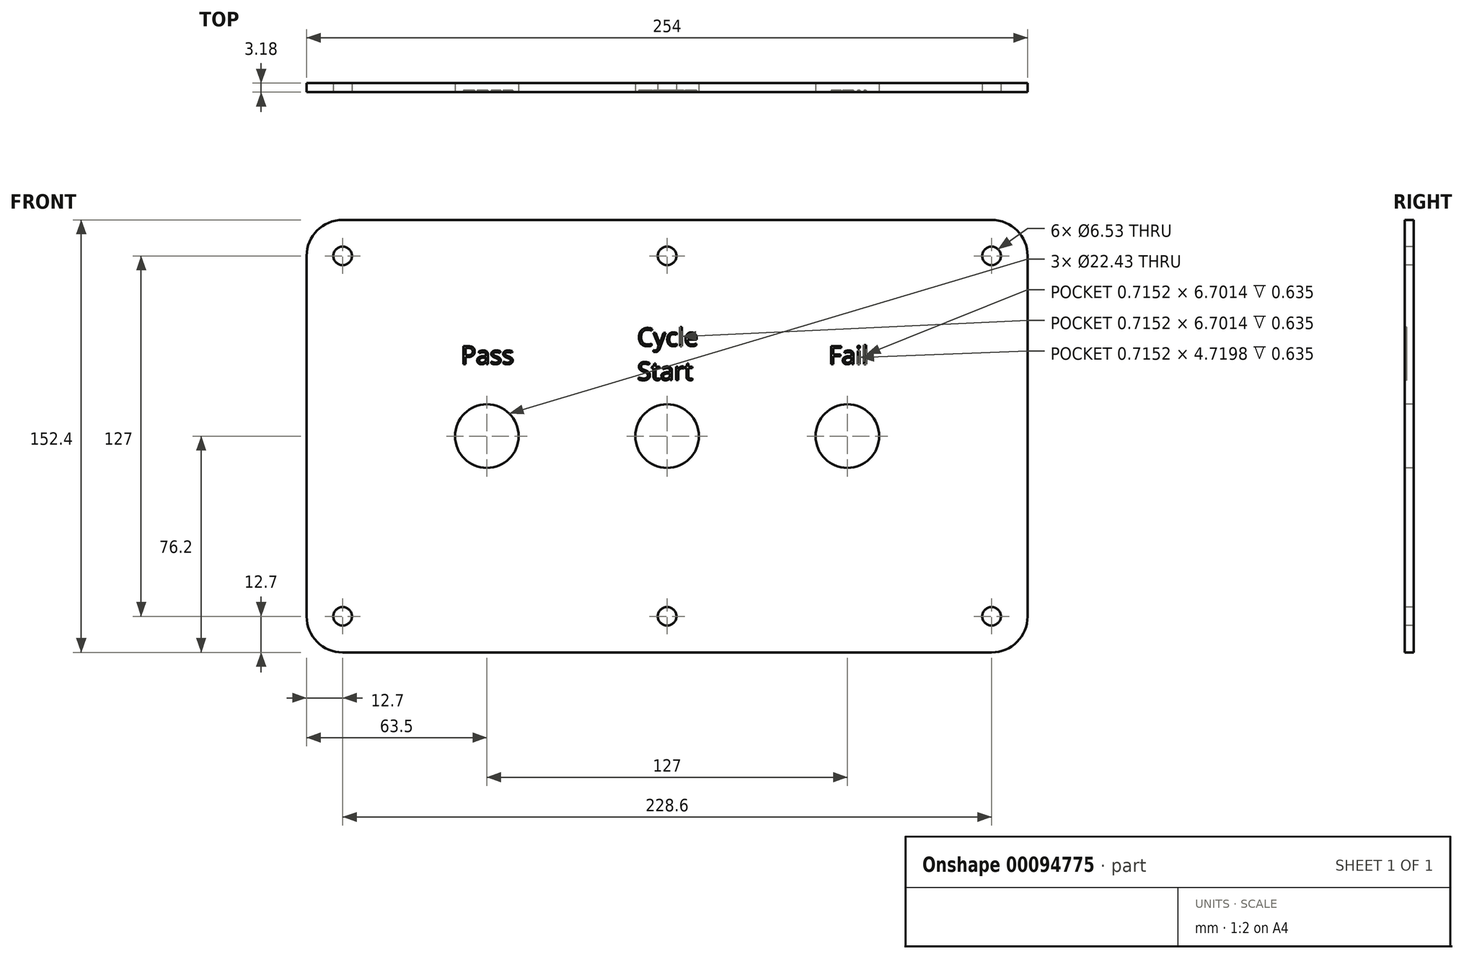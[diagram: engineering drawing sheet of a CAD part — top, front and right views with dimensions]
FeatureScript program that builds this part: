
annotation { "Feature Type Name" : "Feature", "Feature Type Description" : "" }
export const myFeature = defineFeature(function(context is Context, id is Id, definition is map)
    precondition{}
    {
        {
            var Q0;
            Q0=qCreatedBy(makeId("Front.planeOp"),FACE);
            var sketch = newSketch(context, id + "F0", { "sketchPlane" : qUnion([Q0])});
            skLineSegment(sketch, "E0.bottom", {"start": v(-114.3, 76.2) * mm, "end": v(114.3, 76.2) * mm});
            skLineSegment(sketch, "E0.top", {"start": v(-114.3, -76.2) * mm, "end": v(114.3, -76.2) * mm});
            skLineSegment(sketch, "E0.left", {"start": v(-127, 63.5) * mm, "end": v(-127, -63.5) * mm});
            skLineSegment(sketch, "E0.right", {"start": v(127, 63.5) * mm, "end": v(127, -63.5) * mm});
            skPoint(sketch, "E0.middle", {"position": v(0, 0) * mm});
            skPoint(sketch, "E1.visualSharp", {"position": v(-127, 76.2) * mm});
            skArc(sketch, "E1.filletArc", {"start": v(-114.3, 76.2) * mm, "mid": v(-123.28, 72.48) * mm, "end": v(-127, 63.5) * mm});
            skPoint(sketch, "E2.visualSharp", {"position": v(127, 76.2) * mm});
            skArc(sketch, "E2.filletArc", {"start": v(127, 63.5) * mm, "mid": v(123.28, 72.48) * mm, "end": v(114.3, 76.2) * mm});
            skPoint(sketch, "E3.visualSharp", {"position": v(127, -76.2) * mm});
            skArc(sketch, "E3.filletArc", {"start": v(114.3, -76.2) * mm, "mid": v(123.28, -72.48) * mm, "end": v(127, -63.5) * mm});
            skPoint(sketch, "E4.visualSharp", {"position": v(-127, -76.2) * mm});
            skArc(sketch, "E4.filletArc", {"start": v(-127, -63.5) * mm, "mid": v(-123.28, -72.48) * mm, "end": v(-114.3, -76.2) * mm});
            skSolve(sketch);
        }
        {
            var Q0;
            Q0=qSketchRegion(id+"F0",true);
            extrude(context, id + "F1", {"entities" : qUnion([Q0]), "depth" : 3.17 * mm});
        }
        {
            var Q0;
            Q0=makeQuery(id+"F1.opExtrude","CAP_FACE",FACE,{"disambiguationData":[OSD([sQuery(id+"F0.wireOp",EDGE,"E0.bottom"),sQuery(id+"F0.wireOp",EDGE,"E0.top"),sQuery(id+"F0.wireOp",EDGE,"E0.left"),sQuery(id+"F0.wireOp",EDGE,"E0.right")])],"isStart":false});
            var sketch = newSketch(context, id + "F2", { "sketchPlane" : qUnion([Q0])});
            skCircle(sketch, "E5", {"center": v(-63.5, 0) * mm, "radius": 11.21 * mm});
            skCircle(sketch, "E6.1.0.0", {"center": v(0, 0) * mm, "radius": 11.21 * mm});
            skCircle(sketch, "E6.2.0.0", {"center": v(63.5, 0) * mm, "radius": 11.21 * mm});
            skLineSegment(sketch, "E6.direction1", {"start": v(-63.5, 0) * mm, "end": v(0, 0) * mm, "construction": true});
            skSolve(sketch);
        }
        {
            var Q0;
            Q0=qSketchRegion(id+"F2",true);
            extrude(context, id + "F3", {"entities" : qUnion([Q0]), "operationType" : NewBodyOperationType.REMOVE, "oppositeDirection" : true, "depth" : 25.4 * mm});
        }
        {
            var Q0;
            Q0=makeQuery(id+"F1.opExtrude","CAP_FACE",FACE,{"disambiguationData":[OSD([sQuery(id+"F0.wireOp",EDGE,"E0.bottom"),sQuery(id+"F0.wireOp",EDGE,"E0.top"),sQuery(id+"F0.wireOp",EDGE,"E0.left"),sQuery(id+"F0.wireOp",EDGE,"E0.right"),sQuery(id+"F0.wireOp",EDGE,"E1.filletArc"),sQuery(id+"F0.wireOp",EDGE,"E2.filletArc"),sQuery(id+"F0.wireOp",EDGE,"E3.filletArc"),sQuery(id+"F0.wireOp",EDGE,"E4.filletArc")])],"isStart":false});
            var sketch = newSketch(context, id + "F4", { "sketchPlane" : qUnion([Q0])});
            skCircle(sketch, "E7", {"center": v(-114.3, 63.5) * mm, "radius": 3.26 * mm});
            skCircle(sketch, "E8.0.1.0", {"center": v(-114.3, -63.5) * mm, "radius": 3.26 * mm});
            skCircle(sketch, "E8.1.0.0", {"center": v(0, 63.5) * mm, "radius": 3.26 * mm});
            skCircle(sketch, "E8.1.1.0", {"center": v(0, -63.5) * mm, "radius": 3.26 * mm});
            skCircle(sketch, "E8.2.0.0", {"center": v(114.3, 63.5) * mm, "radius": 3.26 * mm});
            skCircle(sketch, "E8.2.1.0", {"center": v(114.3, -63.5) * mm, "radius": 3.26 * mm});
            skLineSegment(sketch, "E8.direction1", {"start": v(-114.3, 63.5) * mm, "end": v(0, 63.5) * mm, "construction": true});
            skLineSegment(sketch, "E8.direction2", {"start": v(-114.3, 63.5) * mm, "end": v(-114.3, -63.5) * mm, "construction": true});
            skSolve(sketch);
        }
        {
            var Q0;
            Q0=qSketchRegion(id+"F4",true);
            extrude(context, id + "F5", {"entities" : qUnion([Q0]), "operationType" : NewBodyOperationType.REMOVE, "oppositeDirection" : true, "depth" : 25.4 * mm});
        }
        {
            var Q0;
            Q0=makeQuery(id+"F1.opExtrude","CAP_FACE",FACE,{"disambiguationData":[OSD([sQuery(id+"F0.wireOp",EDGE,"E0.bottom"),sQuery(id+"F0.wireOp",EDGE,"E0.top"),sQuery(id+"F0.wireOp",EDGE,"E0.left"),sQuery(id+"F0.wireOp",EDGE,"E0.right"),sQuery(id+"F0.wireOp",EDGE,"E1.filletArc"),sQuery(id+"F0.wireOp",EDGE,"E2.filletArc"),sQuery(id+"F0.wireOp",EDGE,"E3.filletArc"),sQuery(id+"F0.wireOp",EDGE,"E4.filletArc")])],"isStart":false});
            var sketch = newSketch(context, id + "F6", { "sketchPlane" : qUnion([Q0])});
            skText(sketch, "E9", { "text": "Pass", "fontName": "OpenSans-Regular.ttf"});
            const initialGuessF6  = {"E9": [-0.07261, 0.0254, 1, 0, 0.00635]};
            skSetInitialGuess(sketch, initialGuessF6);
            skSolve(sketch);
        }
        {
            var Q0;
            {var subQ0=sQuery(id+"F0.wireOp",EDGE,"E4.filletArc");var subQ1=sQuery(id+"F0.wireOp",EDGE,"E3.filletArc");var subQ2=sQuery(id+"F0.wireOp",EDGE,"E2.filletArc");var subQ3=sQuery(id+"F0.wireOp",EDGE,"E1.filletArc");var subQ4=sQuery(id+"F0.wireOp",EDGE,"E0.bottom");var subQ5=sQuery(id+"F0.wireOp",EDGE,"E0.top");var subQ6=sQuery(id+"F0.wireOp",EDGE,"E0.left");var subQ7=sQuery(id+"F0.wireOp",EDGE,"E0.right");Q0=makeQuery(id+"F9.boolean.opBoolean","SPLIT",FACE,{"disambiguationData":[TD([makeQuery(id+"F1.opExtrude","SWEPT_FACE",FACE,{"disambiguationData":[OSD([subQ4])]})])],"derivedFrom":makeQuery(id+"F1.opExtrude","CAP_FACE",FACE,{"disambiguationData":[OSD([subQ4,subQ5,subQ6,subQ7,subQ3,subQ2,subQ1,subQ0])],"isStart":false})});}
            var sketch = newSketch(context, id + "F7", { "sketchPlane" : qUnion([Q0])});
            skText(sketch, "E10", { "text": "Cycle\nStart", "fontName": "OpenSans-Regular.ttf"});
            const initialGuessF7  = {"E10": [-0.01046, 0.03175, 1, 0, 0.00635]};
            skSetInitialGuess(sketch, initialGuessF7);
            skSolve(sketch);
        }
        {
            var Q0;
            {var subQ0=sQuery(id+"F0.wireOp",EDGE,"E0.right");var subQ1=sQuery(id+"F0.wireOp",EDGE,"E1.filletArc");var subQ2=sQuery(id+"F0.wireOp",EDGE,"E4.filletArc");var subQ3=sQuery(id+"F0.wireOp",EDGE,"E3.filletArc");var subQ4=sQuery(id+"F0.wireOp",EDGE,"E2.filletArc");var subQ5=sQuery(id+"F0.wireOp",EDGE,"E0.bottom");var subQ6=sQuery(id+"F0.wireOp",EDGE,"E0.top");var subQ7=sQuery(id+"F0.wireOp",EDGE,"E0.left");Q0=makeQuery(id+"F9.boolean.opBoolean","SPLIT",FACE,{"disambiguationData":[TD([makeQuery(id+"F1.opExtrude","SWEPT_FACE",FACE,{"disambiguationData":[OSD([subQ5])]})])],"derivedFrom":makeQuery(id+"F1.opExtrude","CAP_FACE",FACE,{"disambiguationData":[OSD([subQ5,subQ6,subQ7,subQ0,subQ1,subQ4,subQ3,subQ2])],"isStart":false})});}
            var sketch = newSketch(context, id + "F8", { "sketchPlane" : qUnion([Q0])});
            skText(sketch, "E11", { "text": "Fail", "fontName": "OpenSans-Regular.ttf"});
            const initialGuessF8  = {"E11": [0.05692, 0.0254, 1, 0, 0.00635]};
            skSetInitialGuess(sketch, initialGuessF8);
            skSolve(sketch);
        }
        {
            var Q0;
            Q0 = qSketchRegion(id + "F6", true);
            var Q1;
            Q1 = qSketchRegion(id + "F7", true);
            var Q2;
            Q2 = qSketchRegion(id + "F8", true);
            extrude(context, id + "F9", {"entities" : qUnion([Q0, Q1, Q2]), "operationType" : NewBodyOperationType.REMOVE, "oppositeDirection" : true, "depth" : 0.64 * mm});
        }
    });
